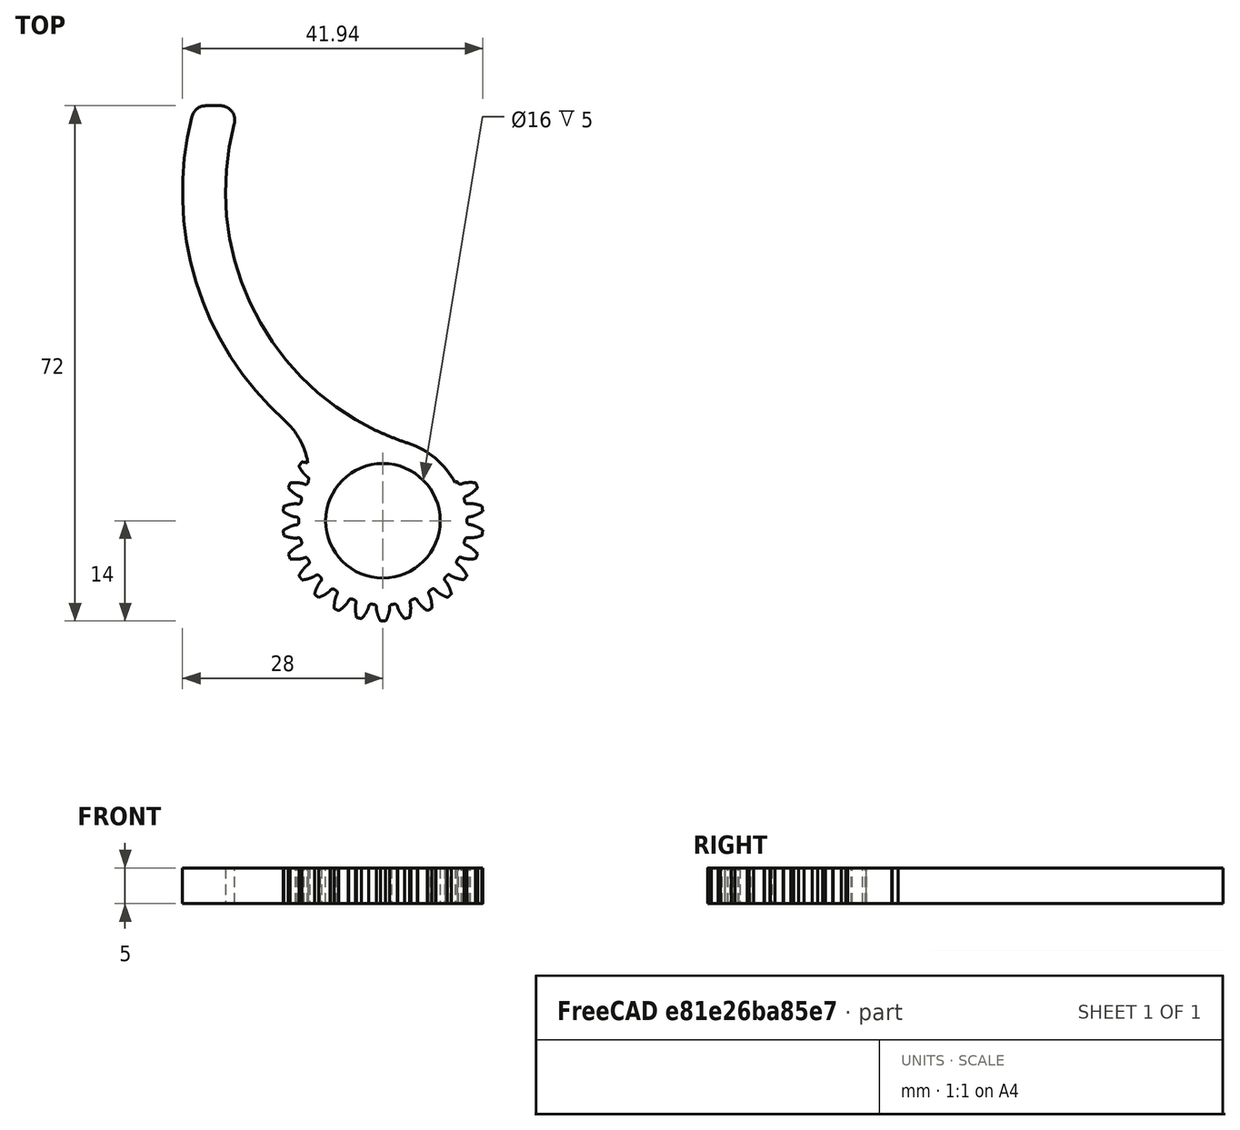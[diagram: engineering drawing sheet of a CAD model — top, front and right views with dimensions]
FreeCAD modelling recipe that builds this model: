
FCSTD DOCUMENT  (FreeCAD 1.0R39109 (Git))
Label: BrasV1_L
License: All rights reserved
LicenseURL: https://en.wikipedia.org/wiki/All_rights_reserved
objects: Sketcher::SketchObject×3, PartDesign::Pad×2, PartDesign::Fillet×2, PartDesign::Pocket×2, PartDesign::Chamfer×1, PartDesign::Line×1, Part::Part2DObjectPython×1, Mesh::Feature×1, PartDesign::CoordinateSystem×1, PartDesign::Body×1
note: 31 computed .brp shape members not serialized (recipe doc carries the construction recipe); baked Part::Feature solids carry a one-line shape summary decoded from their .brp

FEATURE [Sketcher::SketchObject] Sketch
  ArcFitTolerance = 0
  AttachmentSupport = -> [XY_Plane]
  FullyConstrained = true
  MakeInternals = false
  MapMode = 5
  sketch-geometry (5):
    g0: ArcOfCircle CenterX=0 CenterY=0 CenterZ=0 NormalX=0 NormalY=0 NormalZ=1 AngleXU=0 Radius=37 StartAngle=2.8113 EndAngle=4.39717
    g1: Circle CenterX=-15 CenterY=-46 CenterZ=0 NormalX=0 NormalY=0 NormalZ=1 AngleXU=0 Radius=8
    g2: ArcOfCircle CenterX=-15 CenterY=-46 CenterZ=0 NormalX=0 NormalY=0 NormalZ=1 AngleXU=0 Radius=11.3839 StartAngle=2.22683 EndAngle=7.53877
    g3: ArcOfCircle CenterX=0 CenterY=0 CenterZ=0 NormalX=0 NormalY=0 NormalZ=1 AngleXU=0 Radius=43 StartAngle=2.85877 EndAngle=4.17683
    g4: LineSegment StartX=-41.2916 StartY=12 StartZ=0 EndX=-35 EndY=12 EndZ=0
  constraints (14):
    c: Coincident(g0,g-1)
    c: Radius(g0) = 37
    c: Distance(g0,g-2) = 35
    c: Diameter(g1) = 16
    c: Distance(g1,g-2) = 15
    c: Coincident(g2,g1)
    c: Tangent(g2,g0) = 1.5708
    c: Coincident(g3,g0)
    c: Coincident(g2,g3)
    c: Radius(g3) = 43
    c: Coincident(g4,g3)
    c: Coincident(g4,g0)
    c: Horizontal(g4)
    c: Distance(g1,g-1) = 46
FEATURE [PartDesign::Pad] Pad
  Direction = (0,0,1)
  Length = 5
  Length2 = 10
  Midplane = true
  Profile = -> Sketch
  ReferenceAxis = -> Sketch [N_Axis]
  Suppressed = false
  Type = 0
FEATURE [PartDesign::Fillet] Fillet
  Base = -> Pad [Edge8]
  BaseFeature = -> Pad
  Radius = 10
  SupportTransform = false
  Suppressed = false
  UseAllEdges = false
FEATURE [PartDesign::Fillet] Fillet001
  Base = -> Fillet [Edge17,Edge12]
  BaseFeature = -> Fillet
  Radius = 2
  SupportTransform = false
  Suppressed = false
  UseAllEdges = false
FEATURE [PartDesign::Chamfer] Chamfer
  Angle = 45
  Base = -> Fillet001 [Edge24,Edge8]
  BaseFeature = -> Fillet001
  ChamferType = 0
  FlipDirection = false
  Size = 0.8
  Size2 = 1
  SupportTransform = false
  Suppressed = false
  UseAllEdges = false
FEATURE [PartDesign::Line] DatumLine
  AttacherType = Attacher::AttachEngineLine
  AttachmentSupport = -> [Chamfer]
  Length = 20
  MapMode = 42
  Placement = pos=(-15,-46,-1e-16) rot=(0,0,1;0rad)
  ResizeMode = 0
FEATURE [Part::Part2DObjectPython] InvoluteGear  # Draft 2D object (typed FeaturePython)
  AddendumCoefficient = 1
  DedendumCoefficient = 1.25
  ExternalGear = true
  HighPrecision = true
  Modules = 1
  NumberOfTeeth = 26
  Placement = pos=(-15,-46,0) rot=(0,0,1;0.122173rad)
  PressureAngle = 20
  ProfileShiftCoefficient = 0
  RootFilletCoefficient = 0.38
FEATURE [PartDesign::Pad] Pad001
  BaseFeature = -> Chamfer
  Direction = (0,0,1)
  Length = 5
  Length2 = 10
  Midplane = true
  Profile = -> InvoluteGear
  ReferenceAxis = -> InvoluteGear [N_Axis]
  Suppressed = false
  Type = 0
FEATURE [Sketcher::SketchObject] Sketch001
  ArcFitTolerance = 0
  AttachmentSupport = -> [Pad001]
  FullyConstrained = false
  MakeInternals = false
  MapMode = 5
  Placement = pos=(0,0,2.5) rot=(0,0,1;0rad)
  sketch-geometry (1):
    g0: Circle CenterX=-15 CenterY=-46 CenterZ=0 NormalX=0 NormalY=0 NormalZ=1 AngleXU=0 Radius=8
  constraints (1):
    c: Diameter(g0) = 16
FEATURE [PartDesign::Pocket] Pocket
  BaseFeature = -> Pad001
  Direction = (0,0,-1)
  Length = 5
  Length2 = 5
  Profile = -> Sketch001
  ReferenceAxis = -> Sketch001 [N_Axis]
  Suppressed = false
  Type = 1
FEATURE [Sketcher::SketchObject] Sketch002
  ArcFitTolerance = 0
  AttachmentSupport = -> [Pocket]
  ExternalGeometry = -> [Pocket]
  FullyConstrained = true
  MakeInternals = false
  MapMode = 5
  Placement = pos=(0,0,2.5) rot=(0,0,1;0rad)
  sketch-geometry (4):
    g0: ArcOfCircle CenterX=-15 CenterY=-46 CenterZ=0 NormalX=0 NormalY=0 NormalZ=1 AngleXU=0 Radius=11.4 StartAngle=0.488692 EndAngle=1.25558
    g1: ArcOfCircle CenterX=0 CenterY=0 CenterZ=0 NormalX=0 NormalY=0 NormalZ=1 AngleXU=0 Radius=36.9839 StartAngle=4.1662 EndAngle=4.39717
    g2: ArcOfCircle CenterX=-15 CenterY=-46 CenterZ=0 NormalX=0 NormalY=0 NormalZ=1 AngleXU=0 Radius=15 StartAngle=0.488692 EndAngle=1.85533
    g3: LineSegment StartX=-4.9344 StartY=-40.648 StartZ=0 EndX=-1.75579 EndY=-38.9579 EndZ=0
  constraints (11):
    c: Coincident(g1,g-1)
    c: Coincident(g2,g0)
    c: Coincident(g2,g1)
    c: Coincident(g3,g0)
    c: Coincident(g3,g2)
    c: Radius(g0) = 11.4
    c: Tangent(g1,g0) = 1.5708
    c: Coincident(g0,g-3)
    c: Radius(g2) = 15
    c: Perpendicular(g0,g3)
    c: Angle(g-1,g3) = 0.488692
FEATURE [PartDesign::Pocket] Pocket001
  BaseFeature = -> Pocket
  Direction = (0,0,-1)
  Length = 5
  Length2 = 5
  Profile = -> Sketch002
  ReferenceAxis = -> Sketch002 [N_Axis]
  Suppressed = false
  Type = 0
FEATURE [Mesh::Feature] Mesh  label="Corps (Meshed)"
FEATURE [PartDesign::CoordinateSystem] LCS_1
  AttacherType = Attacher::AttachEngine3D
  AttachmentSupport = -> [Pocket001]
  MapMode = 11
  Placement = pos=(-15,-46,2.5) rot=(0,0,1;1.5708rad)
FEATURE [PartDesign::Body] Body  label="bras_L"
  AllowCompound = false
  Group = -> [Sketch,Pad,Fillet,Fillet001,Chamfer,DatumLine,InvoluteGear,Pad001,Sketch001,Pocket,Sketch002,Pocket001,LCS_1]
  Origin = -> Origin
  Tip = -> Pocket001
